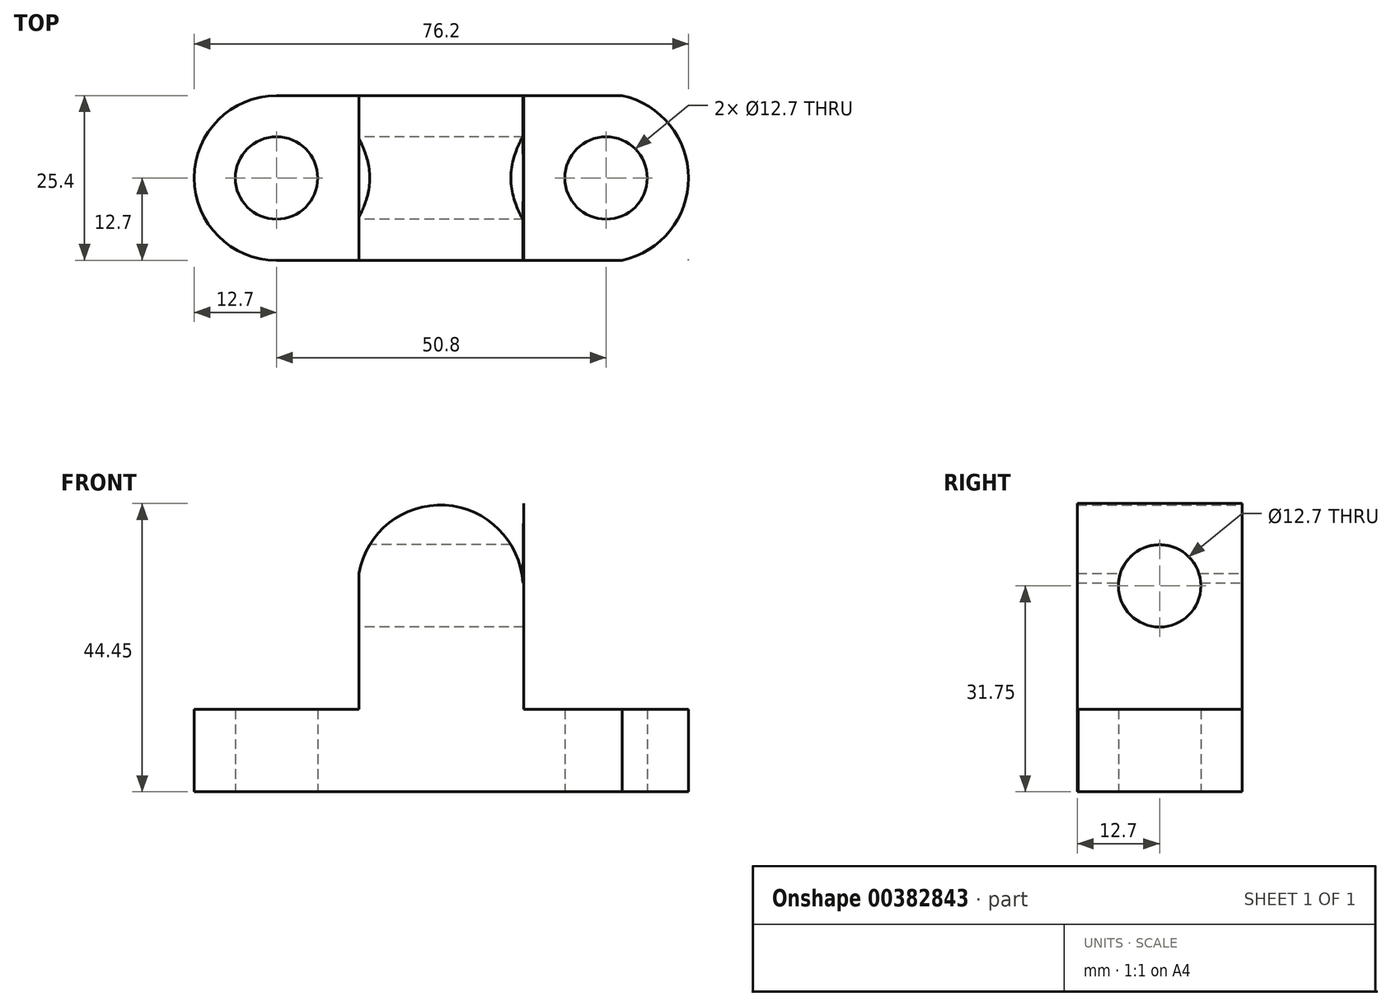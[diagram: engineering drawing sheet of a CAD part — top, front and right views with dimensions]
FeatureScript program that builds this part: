
annotation { "Feature Type Name" : "Feature", "Feature Type Description" : "" }
export const myFeature = defineFeature(function(context is Context, id is Id, definition is map)
    precondition{}
    {
        {
            var Q0;
            Q0=qCreatedBy(makeId("Front.planeOp"),FACE);
            var sketch = newSketch(context, id + "F0", { "sketchPlane" : qUnion([Q0])});
            skLineSegment(sketch, "E0", {"start": v(0, 0) * mm, "end": v(76.2, 0) * mm});
            skLineSegment(sketch, "E1", {"start": v(76.2, 0) * mm, "end": v(76.2, 12.7) * mm});
            skLineSegment(sketch, "E2", {"start": v(76.2, 12.7) * mm, "end": v(50.8, 12.7) * mm});
            skLineSegment(sketch, "E3", {"start": v(50.8, 12.7) * mm, "end": v(50.8, 44.45) * mm});
            skLineSegment(sketch, "E4", {"start": v(50.8, 44.45) * mm, "end": v(25.4, 44.45) * mm});
            skLineSegment(sketch, "E5", {"start": v(25.4, 44.45) * mm, "end": v(25.4, 12.7) * mm});
            skLineSegment(sketch, "E6", {"start": v(25.4, 12.7) * mm, "end": v(0, 12.7) * mm});
            skLineSegment(sketch, "E7", {"start": v(0, 12.7) * mm, "end": v(0, 0) * mm});
            skSolve(sketch);
        }
        {
            var Q0;
            Q0 = qSketchRegion(id + "F0", true);
            extrude(context, id + "F1", {"entities" : qUnion([Q0]), "depth" : 25.4 * mm});
        }
        {
            var Q0;
            Q0=qCreatedBy(makeId("Top.planeOp"),FACE);
            var sketch = newSketch(context, id + "F2", { "sketchPlane" : qUnion([Q0])});
            skCircle(sketch, "E8", {"center": v(12.7, -12.7) * mm, "radius": 6.35 * mm});
            skCircle(sketch, "E9", {"center": v(63.5, -12.7) * mm, "radius": 6.35 * mm});
            skSolve(sketch);
        }
        {
            var Q0;
            Q0 = qSketchRegion(id + "F2", true);
            extrude(context, id + "F3", {"entities" : qUnion([Q0]), "operationType" : NewBodyOperationType.REMOVE, "depth" : 25.4 * mm});
        }
        {
            var Q0;
            Q0=qCreatedBy(makeId("Right.planeOp"),FACE);
            var sketch = newSketch(context, id + "F4", { "sketchPlane" : qUnion([Q0])});
            skCircle(sketch, "E10", {"center": v(-12.7, 31.75) * mm, "radius": 6.24 * mm});
            skSolve(sketch);
        }
        {
            var Q0;
            Q0 = qSketchRegion(id + "F4", true);
            extrude(context, id + "F5", {"entities" : qUnion([Q0]), "operationType" : NewBodyOperationType.REMOVE, "depth" : 25.4 * mm});
        }
        {
            var Q0;
            Q0=makeQuery(id+"F1.opExtrude","SWEPT_FACE",FACE,{"disambiguationData":[OSD([sQuery(id+"F0.wireOp",EDGE,"E5")])]});
            var sketch = newSketch(context, id + "F6", { "sketchPlane" : qUnion([Q0])});
            skCircle(sketch, "E11", {"center": v(12.7, 31.75) * mm, "radius": 6.35 * mm});
            skSolve(sketch);
        }
        {
            var Q0;
            Q0 = qSketchRegion(id + "F6", true);
            extrude(context, id + "F7", {"entities" : qUnion([Q0]), "operationType" : NewBodyOperationType.REMOVE, "oppositeDirection" : true, "depth" : 25.4 * mm});
        }
        {
            var Q0;
            Q0=qCreatedBy(makeId("Top.planeOp"),FACE);
            var sketch = newSketch(context, id + "F8", { "sketchPlane" : qUnion([Q0])});
            skArc(sketch, "E12", {"start": v(12.7, 0) * mm, "mid": v(0, -12.7) * mm, "end": v(12.7, -25.4) * mm});
            skLineSegment(sketch, "E13", {"start": v(12.7, -25.4) * mm, "end": v(0, -25.4) * mm});
            skLineSegment(sketch, "E14", {"start": v(0, -25.4) * mm, "end": v(0, 0) * mm});
            skLineSegment(sketch, "E15", {"start": v(0, 0) * mm, "end": v(12.7, 0) * mm});
            skSolve(sketch);
        }
        {
            var Q0;
            Q0 = qSketchRegion(id + "F8", true);
            extrude(context, id + "F9", {"entities" : qUnion([Q0]), "operationType" : NewBodyOperationType.REMOVE, "depth" : 25.4 * mm});
        }
        {
            var Q0;
            Q0=qCreatedBy(makeId("Top.planeOp"),FACE);
            var sketch = newSketch(context, id + "F10", { "sketchPlane" : qUnion([Q0])});
            skArc(sketch, "E16", {"start": v(66, -25.4) * mm, "mid": v(76.2, -12.7) * mm, "end": v(66, 0) * mm});
            skLineSegment(sketch, "E17", {"start": v(66, 0) * mm, "end": v(76.21, 0) * mm});
            skLineSegment(sketch, "E18", {"start": v(76.21, 0) * mm, "end": v(76.2, -25.4) * mm});
            skLineSegment(sketch, "E19", {"start": v(76.2, -25.4) * mm, "end": v(66, -25.4) * mm});
            skSolve(sketch);
        }
        {
            var Q0;
            Q0 = qSketchRegion(id + "F10", true);
            extrude(context, id + "F11", {"entities" : qUnion([Q0]), "operationType" : NewBodyOperationType.REMOVE, "depth" : 25.4 * mm});
        }
        {
            var Q0;
            Q0=qCreatedBy(makeId("Front.planeOp"),FACE);
            var sketch = newSketch(context, id + "F12", { "sketchPlane" : qUnion([Q0])});
            skArc(sketch, "E20", {"start": v(50.65, 32.2) * mm, "mid": v(38.06, 44.22) * mm, "end": v(25.25, 32.44) * mm});
            skLineSegment(sketch, "E21", {"start": v(25.25, 32.44) * mm, "end": v(25.4, 44.45) * mm});
            skLineSegment(sketch, "E22", {"start": v(25.4, 44.45) * mm, "end": v(50.8, 44.45) * mm});
            skLineSegment(sketch, "E23", {"start": v(50.8, 44.45) * mm, "end": v(50.65, 32.2) * mm});
            skSolve(sketch);
        }
        {
            var Q0;
            Q0 = qSketchRegion(id + "F12", true);
            extrude(context, id + "F13", {"entities" : qUnion([Q0]), "operationType" : NewBodyOperationType.REMOVE, "depth" : 25.4 * mm});
        }
    });
